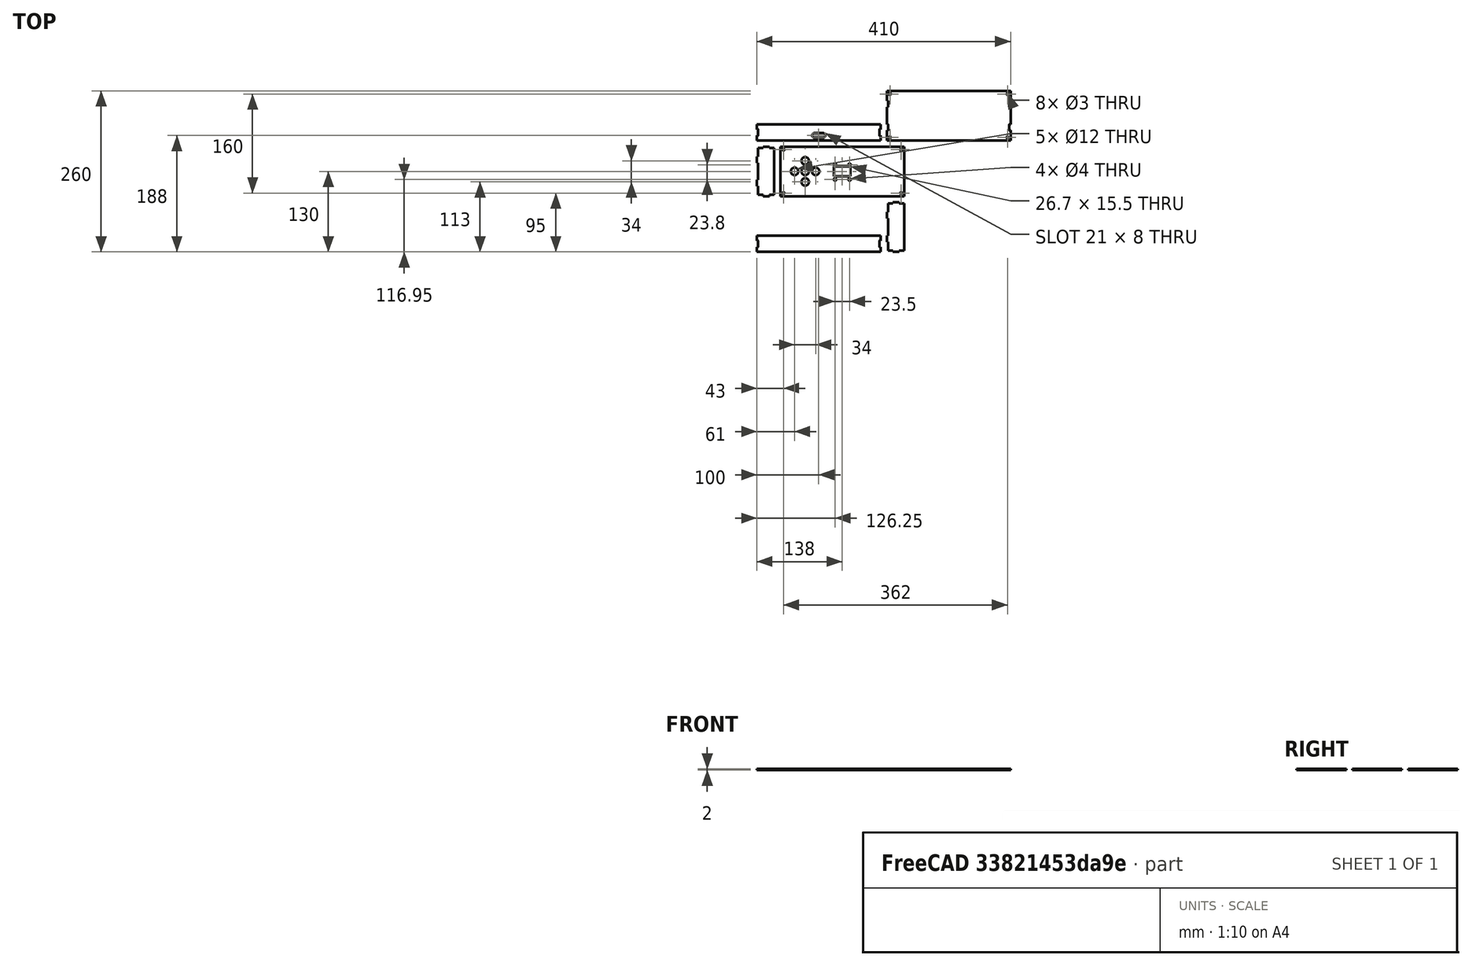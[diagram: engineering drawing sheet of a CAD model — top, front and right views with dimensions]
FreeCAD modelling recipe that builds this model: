
FCSTD DOCUMENT  (FreeCAD 1.0R39109 (Git))
Label: export_shape1
License: All rights reserved
LicenseURL: http://en.wikipedia.org/wiki/All_rights_reserved
objects: Part::Feature×6, Part::Part2DObjectPython×6
note: 12 computed .brp shape members not serialized (recipe doc carries the construction recipe); baked Part::Feature solids carry a one-line shape summary decoded from their .brp

FEATURE [Part::Feature] test
  Placement = pos=(100,13,-8) rot=(-1,0,0;1.5708rad)
  shape: bbox 200 x 26 x 2 mm, 18 faces (baked)
FEATURE [Part::Feature] test001
  Placement = pos=(225,40,130) rot=(0,1,0;1.5708rad)
  shape: bbox 28 x 80 x 2 mm, 22 faces (baked)
FEATURE [Part::Feature] test002
  Placement = pos=(15,130,-68) rot=(0,1,0;1.5708rad)
  shape: bbox 28 x 80 x 2 mm, 22 faces (baked)
FEATURE [Part::Feature] test003
  Placement = pos=(138,130,45) rot=(0,-1,0;3.14159rad)
  shape: bbox 200 x 80 x 2 mm, 23 faces (baked)
FEATURE [Part::Feature] test004
  Placement = pos=(100,193,70) rot=(-1,0,0;1.5708rad)
  shape: bbox 200 x 26 x 2 mm, 22 faces (baked)
FEATURE [Part::Feature] test005
  Placement = pos=(310,220,17) rot=(0,-1,0;3.14159rad)
  shape: bbox 200 x 80 x 2 mm, 34 faces (baked)
FEATURE [Part::Part2DObjectPython] Shape2DView  # Draft 2D object (typed FeaturePython)
  AutoUpdate = true
  Base = -> test
  Clip = false
  FuseArch = false
  HiddenLines = false
  InPlace = true
  OnlySolids = false
  Projection = (0,0,1)
  ProjectionMode = 0
  SegmentLength = 0.05
  Tessellation = false
  VisibleOnly = false
FEATURE [Part::Part2DObjectPython] Shape2DView001  # Draft 2D object (typed FeaturePython)
  AutoUpdate = true
  Base = -> test001
  Clip = false
  FuseArch = false
  HiddenLines = false
  InPlace = true
  OnlySolids = false
  Projection = (0,0,1)
  ProjectionMode = 0
  SegmentLength = 0.05
  Tessellation = false
  VisibleOnly = false
FEATURE [Part::Part2DObjectPython] Shape2DView002  # Draft 2D object (typed FeaturePython)
  AutoUpdate = true
  Base = -> test002
  Clip = false
  FuseArch = false
  HiddenLines = false
  InPlace = true
  OnlySolids = false
  Projection = (0,0,1)
  ProjectionMode = 0
  SegmentLength = 0.05
  Tessellation = false
  VisibleOnly = false
FEATURE [Part::Part2DObjectPython] Shape2DView003  # Draft 2D object (typed FeaturePython)
  AutoUpdate = true
  Base = -> test003
  Clip = false
  FuseArch = false
  HiddenLines = false
  InPlace = true
  OnlySolids = false
  Projection = (0,0,1)
  ProjectionMode = 0
  SegmentLength = 0.05
  Tessellation = false
  VisibleOnly = false
FEATURE [Part::Part2DObjectPython] Shape2DView004  # Draft 2D object (typed FeaturePython)
  AutoUpdate = true
  Base = -> test004
  Clip = false
  FuseArch = false
  HiddenLines = false
  InPlace = true
  OnlySolids = false
  Projection = (0,0,1)
  ProjectionMode = 0
  SegmentLength = 0.05
  Tessellation = false
  VisibleOnly = false
FEATURE [Part::Part2DObjectPython] Shape2DView005  # Draft 2D object (typed FeaturePython)
  AutoUpdate = true
  Base = -> test005
  Clip = false
  FuseArch = false
  HiddenLines = false
  InPlace = true
  OnlySolids = false
  Projection = (0,0,1)
  ProjectionMode = 0
  SegmentLength = 0.05
  Tessellation = false
  VisibleOnly = false
